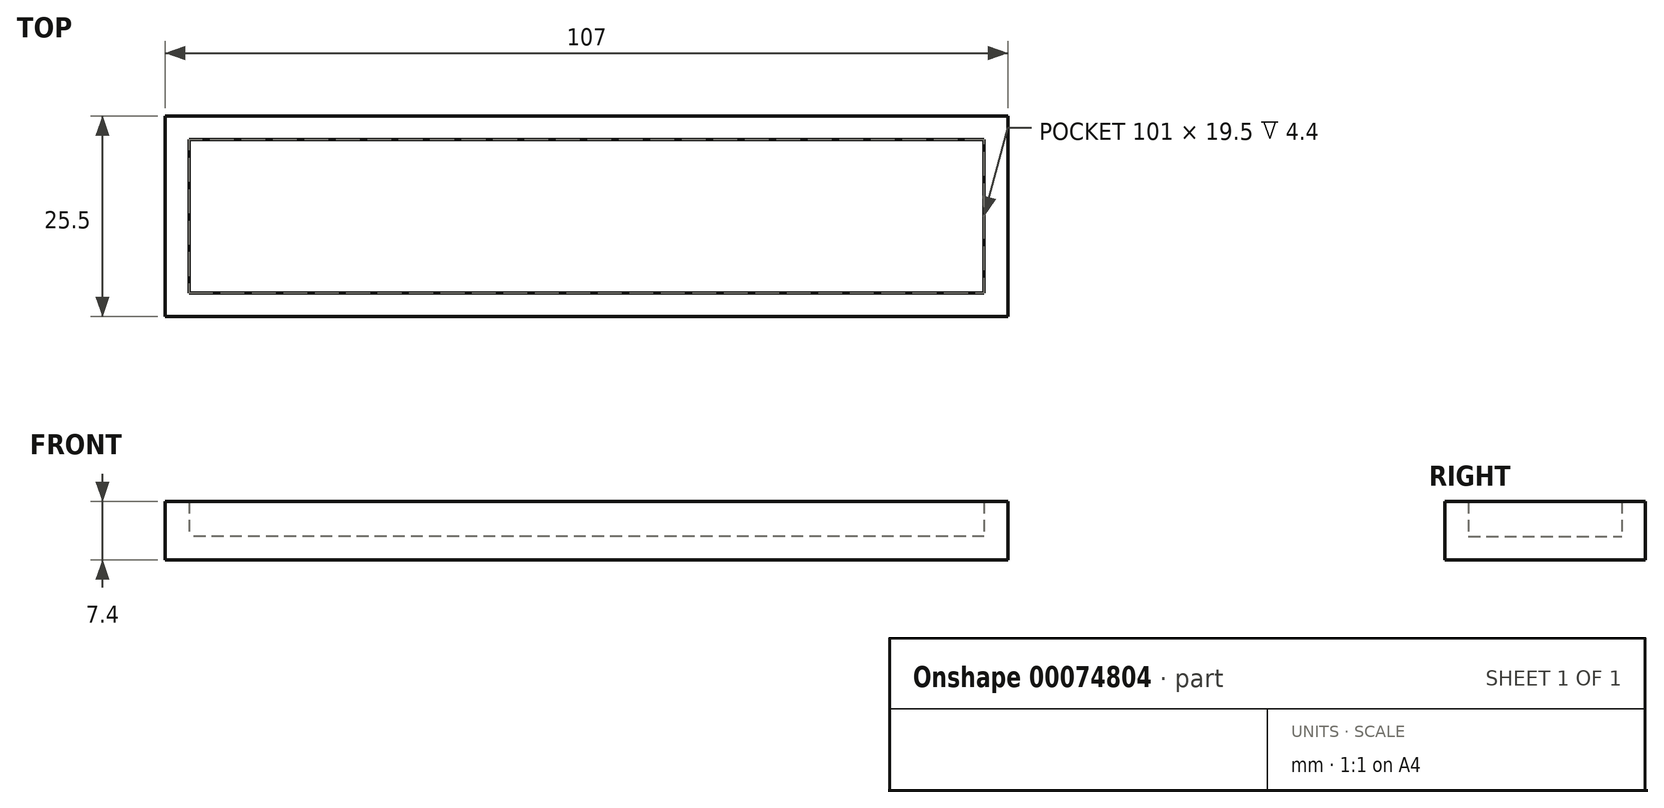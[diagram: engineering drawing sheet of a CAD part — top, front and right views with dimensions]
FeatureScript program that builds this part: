
annotation { "Feature Type Name" : "Feature", "Feature Type Description" : "" }
export const myFeature = defineFeature(function(context is Context, id is Id, definition is map)
    precondition{}
    {
        {
            var Q0;
            Q0=qCreatedBy(makeId("Top.planeOp"),FACE);
            var sketch = newSketch(context, id + "F0", { "sketchPlane" : qUnion([Q0])});
            skLineSegment(sketch, "E0.rect.bottom", {"start": v(53.5, -12.75) * mm, "end": v(-53.5, -12.75) * mm});
            skLineSegment(sketch, "E0.rect.top", {"start": v(53.5, 12.75) * mm, "end": v(-53.5, 12.75) * mm});
            skLineSegment(sketch, "E0.rect.left", {"start": v(53.5, -12.75) * mm, "end": v(53.5, 12.75) * mm});
            skLineSegment(sketch, "E0.rect.right", {"start": v(-53.5, -12.75) * mm, "end": v(-53.5, 12.75) * mm});
            skPoint(sketch, "E0.rect.middle", {"position": v(0, 0) * mm});
            skLineSegment(sketch, "E1.rect.bottom", {"start": v(50.5, -9.75) * mm, "end": v(-50.5, -9.75) * mm});
            skLineSegment(sketch, "E1.rect.top", {"start": v(50.5, 9.75) * mm, "end": v(-50.5, 9.75) * mm});
            skLineSegment(sketch, "E1.rect.left", {"start": v(50.5, -9.75) * mm, "end": v(50.5, 9.75) * mm});
            skLineSegment(sketch, "E1.rect.right", {"start": v(-50.5, -9.75) * mm, "end": v(-50.5, 9.75) * mm});
            skSolve(sketch);
        }
        {
            var Q0;
            Q0=makeQuery(id+"F0.imprint","IMPRINT",FACE,{"disambiguationData":[TD([[makeQuery(id+"F0.imprint","IMPRINT",EDGE,{"derivedFrom":sQuery(id+"F0.wireOp",EDGE,"E0.rect.bottom")}),-1.0]])]});
            var Q1;
            Q1=makeQuery(id+"F0.imprint","IMPRINT",FACE,{"disambiguationData":[TD([[makeQuery(id+"F0.imprint","IMPRINT",EDGE,{"derivedFrom":sQuery(id+"F0.wireOp",EDGE,"E1.rect.bottom")}),-1.0]])]});
            extrude(context, id + "F1", {"entities" : qUnion([Q0, Q1]), "oppositeDirection" : true, "depth" : 3 * mm});
        }
        {
            var Q0;
            Q0 = qSketchRegion(id + "F0", true);
            extrude(context, id + "F2", {"entities" : qUnion([Q0]), "operationType" : NewBodyOperationType.ADD, "depth" : 4.4 * mm});
        }
    });
